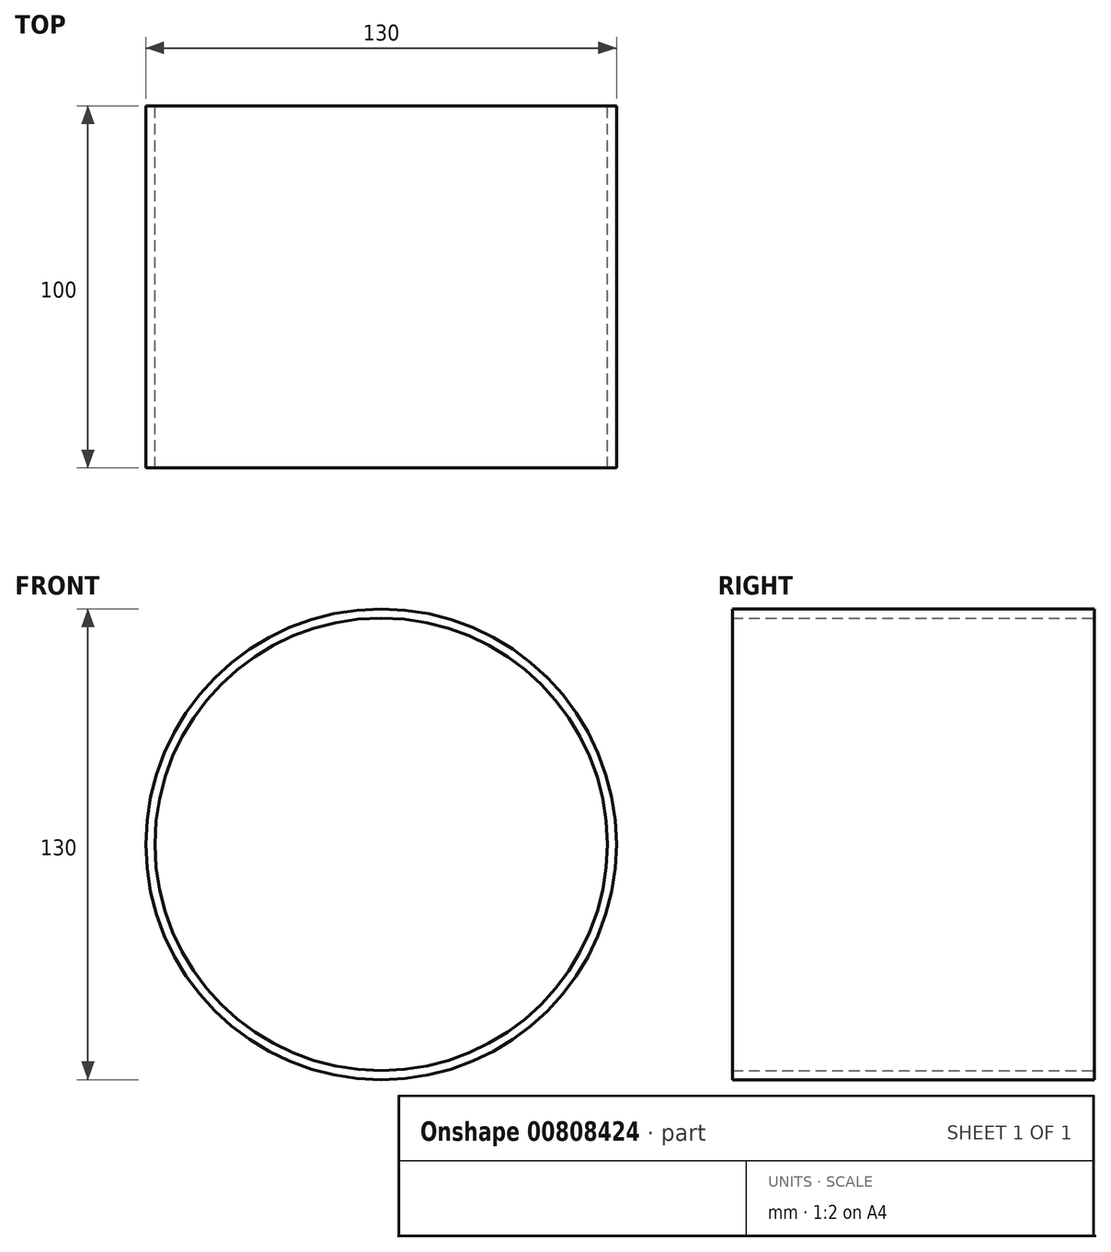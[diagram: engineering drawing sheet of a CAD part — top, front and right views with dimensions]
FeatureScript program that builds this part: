
annotation { "Feature Type Name" : "Feature", "Feature Type Description" : "" }
export const myFeature = defineFeature(function(context is Context, id is Id, definition is map)
    precondition{}
    {
        {
            var Q0;
            Q0=qCreatedBy(makeId("Front.planeOp"),FACE);
            var sketch = newSketch(context, id + "F0", { "sketchPlane" : qUnion([Q0])});
            skCircle(sketch, "E0", {"center": v(0, 0) * mm, "radius": 65 * mm});
            skCircle(sketch, "E1", {"center": v(0, 0) * mm, "radius": 62.5 * mm});
            skSolve(sketch);
        }
        {
            var Q0;
            Q0=makeQuery(id+"F0.imprint","IMPRINT",FACE,{"disambiguationData":[TD([[makeQuery(id+"F0.imprint","IMPRINT",EDGE,{"derivedFrom":sQuery(id+"F0.wireOp",EDGE,"E0")}),1.0]])]});
            extrude(context, id + "F1", {"entities" : qUnion([Q0]), "depth" : 100 * mm, "offsetDistance" : 25 * mm});
        }
    });
